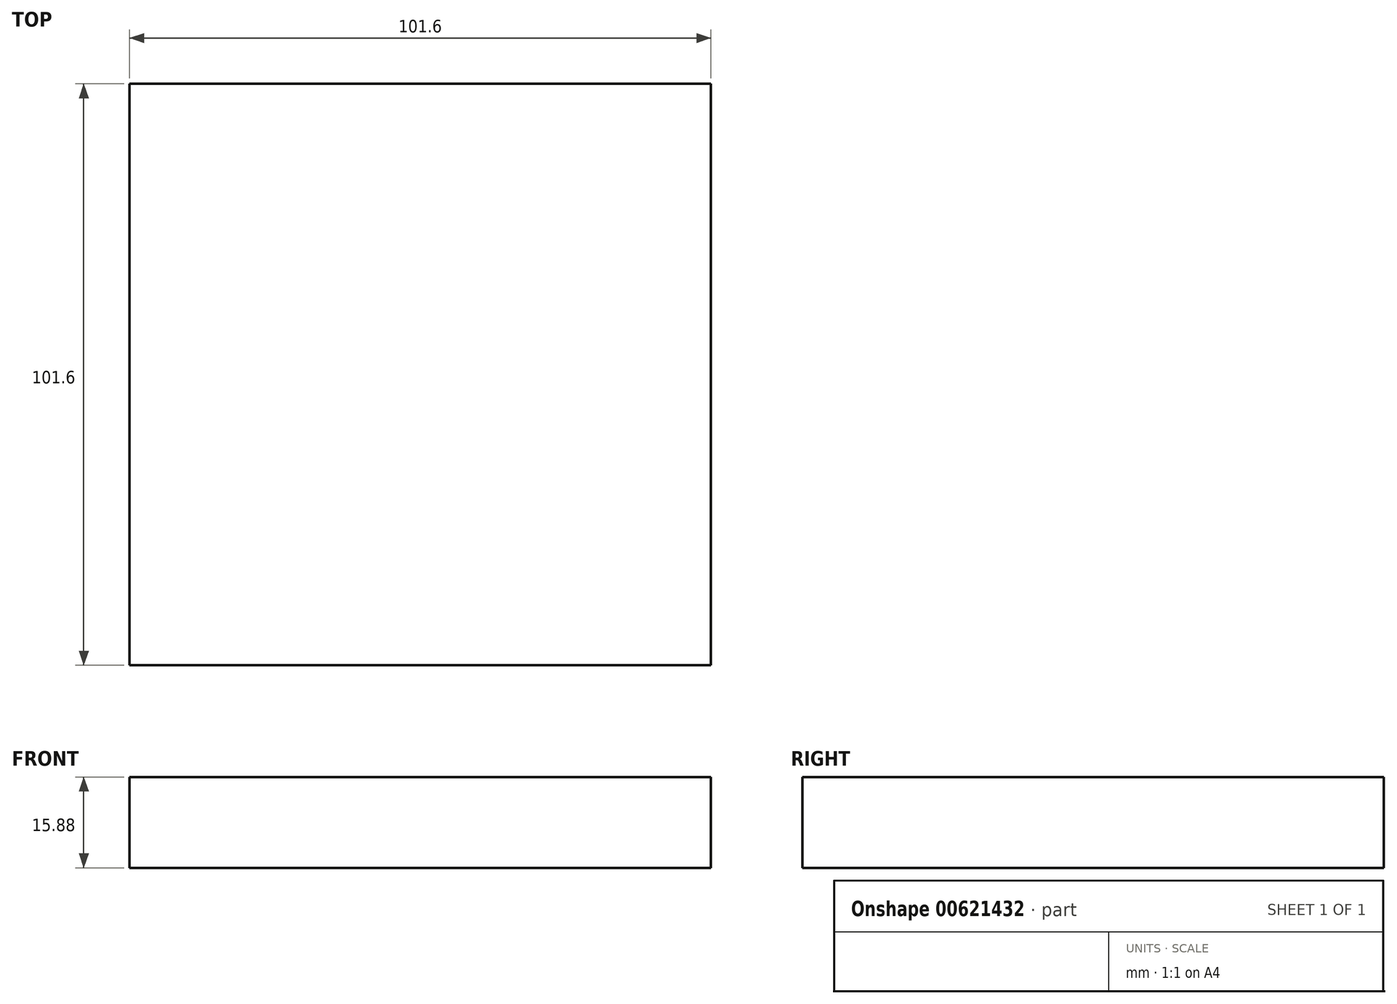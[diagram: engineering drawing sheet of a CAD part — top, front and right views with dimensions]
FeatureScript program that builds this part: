
annotation { "Feature Type Name" : "Feature", "Feature Type Description" : "" }
export const myFeature = defineFeature(function(context is Context, id is Id, definition is map)
    precondition{}
    {
        {
            var Q0;
            Q0=qCreatedBy(makeId("Front.planeOp"),FACE);
            var sketch = newSketch(context, id + "F0", { "sketchPlane" : qUnion([Q0])});
            skLineSegment(sketch, "E0.bottom", {"start": v(0, 0) * mm, "end": v(101.6, 0) * mm});
            skLineSegment(sketch, "E0.top", {"start": v(0, 15.88) * mm, "end": v(101.6, 15.88) * mm});
            skLineSegment(sketch, "E0.left", {"start": v(0, 0) * mm, "end": v(0, 15.88) * mm});
            skLineSegment(sketch, "E0.right", {"start": v(101.6, 0) * mm, "end": v(101.6, 15.88) * mm});
            skSolve(sketch);
        }
        {
            var Q0;
            Q0=makeQuery(id+"F0.imprint","IMPRINT",FACE,{"disambiguationData":[TD([[makeQuery(id+"F0.imprint","IMPRINT",EDGE,{"derivedFrom":sQuery(id+"F0.wireOp",EDGE,"E0.bottom")}),1.0]])]});
            extrude(context, id + "F1", {"entities" : qUnion([Q0]), "oppositeDirection" : true, "depth" : 101.6 * mm, "offsetDistance" : 25.4 * mm});
        }
    });
